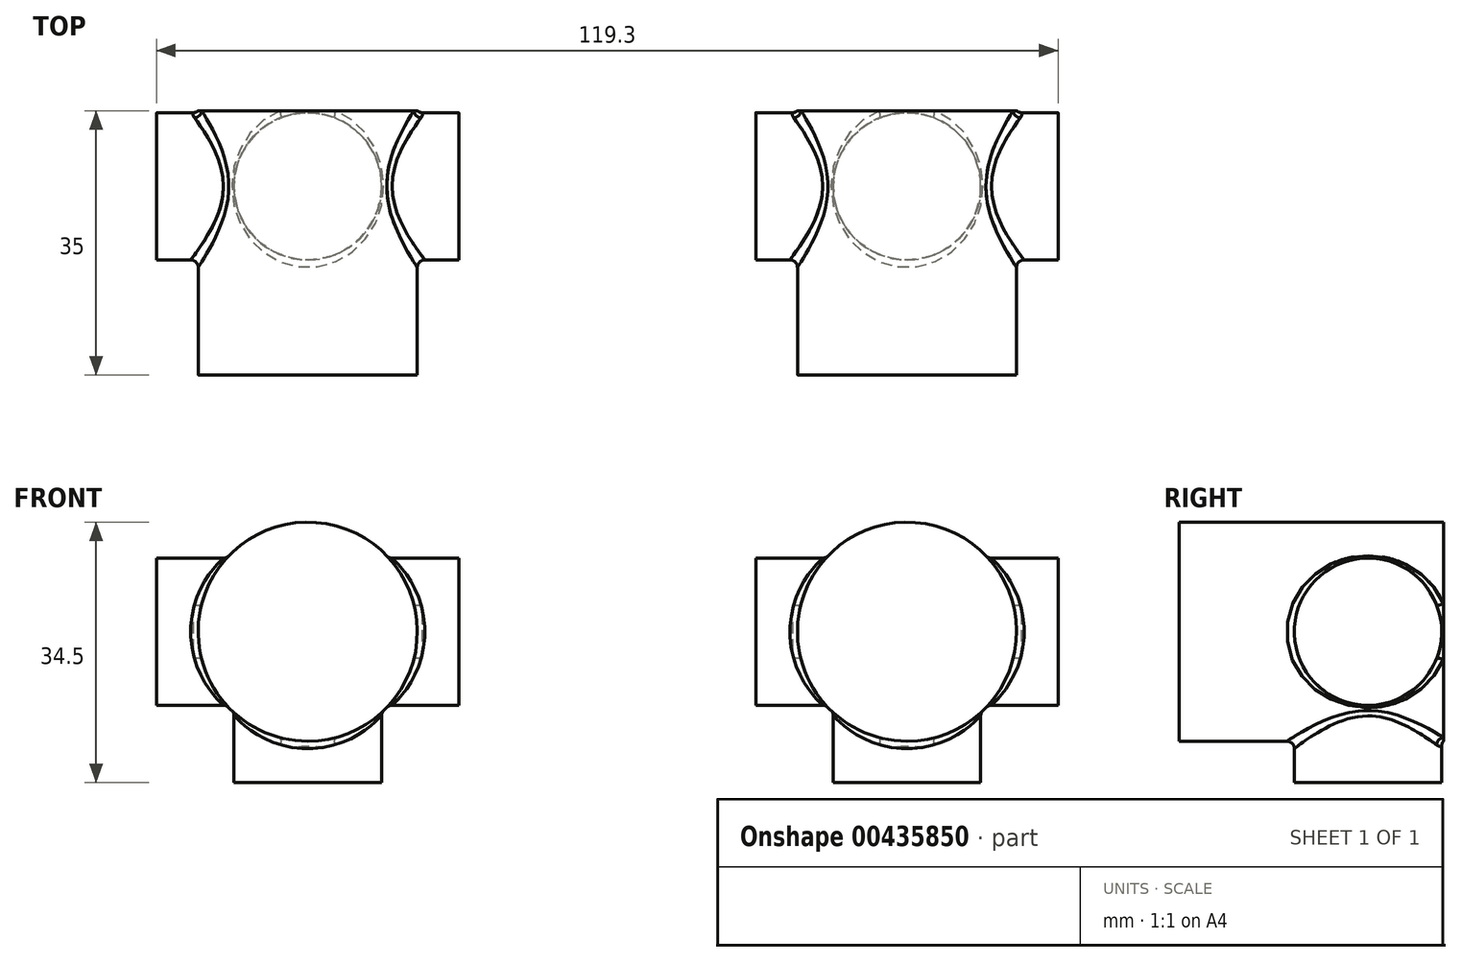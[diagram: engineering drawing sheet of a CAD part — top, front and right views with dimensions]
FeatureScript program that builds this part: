
annotation { "Feature Type Name" : "Feature", "Feature Type Description" : "" }
export const myFeature = defineFeature(function(context is Context, id is Id, definition is map)
    precondition{}
    {
        {
            var Q0;
            Q0=qCreatedBy(makeId("Front.planeOp"),FACE);
            var sketch = newSketch(context, id + "F0", { "sketchPlane" : qUnion([Q0])});
            skCircle(sketch, "E0", {"center": v(0, 0) * mm, "radius": 14.5 * mm});
            skSolve(sketch);
        }
        {
            var Q0;
            Q0 = qSketchRegion(id + "F0", true);
            extrude(context, id + "F1", {"entities" : qUnion([Q0]), "depth" : 25 * mm, "hasSecondDirection" : true, "secondDirectionOppositeDirection" : true, "secondDirectionDepth" : 10 * mm});
        }
        {
            var Q0;
            Q0=qCreatedBy(makeId("Right.planeOp"),FACE);
            var sketch = newSketch(context, id + "F2", { "sketchPlane" : qUnion([Q0])});
            skCircle(sketch, "E1", {"center": v(0, 0) * mm, "radius": 9.75 * mm});
            skSolve(sketch);
        }
        {
            var Q0;
            Q0 = qSketchRegion(id + "F2", true);
            extrude(context, id + "F3", {"entities" : qUnion([Q0]), "operationType" : NewBodyOperationType.ADD, "depth" : 20 * mm, "hasSecondDirection" : true, "secondDirectionOppositeDirection" : true, "secondDirectionDepth" : 20 * mm});
        }
        {
            var Q0;
            Q0=qCreatedBy(makeId("Top.planeOp"),FACE);
            var sketch = newSketch(context, id + "F4", { "sketchPlane" : qUnion([Q0])});
            skCircle(sketch, "E2", {"center": v(0, 0) * mm, "radius": 9.75 * mm});
            skSolve(sketch);
        }
        {
            var Q0;
            Q0 = qSketchRegion(id + "F4", true);
            extrude(context, id + "F5", {"entities" : qUnion([Q0]), "operationType" : NewBodyOperationType.ADD, "oppositeDirection" : true, "depth" : 20 * mm});
        }
        {
            var Q0;
            Q0=makeQuery(id+"F5.boolean.opBoolean","INTERSECT",EDGE,{"disambiguationData":[OD(2.0)],"derivedFrom":[makeQuery(id+"F1.opExtrude","SWEPT_FACE",FACE,{"disambiguationData":[OSD([sQuery(id+"F0.wireOp",EDGE,"E0")])]}),makeQuery(id+"F5.opExtrude","SWEPT_FACE",FACE,{"disambiguationData":[OSD([sQuery(id+"F4.wireOp",EDGE,"E2")])]})]});
            var Q1;
            Q1=makeQuery(id+"F5.boolean.opBoolean","SPLIT",EDGE,{"disambiguationData":[OD(1.0)],"derivedFrom":makeQuery(id+"F3.boolean.opBoolean","INTERSECT",EDGE,{"disambiguationData":[OD(0.0)],"derivedFrom":[makeQuery(id+"F1.opExtrude","SWEPT_FACE",FACE,{"disambiguationData":[OSD([sQuery(id+"F0.wireOp",EDGE,"E0")])]}),makeQuery(id+"F3.opExtrude","SWEPT_FACE",FACE,{"disambiguationData":[OSD([sQuery(id+"F2.wireOp",EDGE,"E1")])]})]})});
            var Q2;
            {var subQ1=sQuery(id+"F2.wireOp",EDGE,"E1");Q2=makeQuery(id+"F5.boolean.opBoolean","INTERSECT",EDGE,{"derivedFrom":[makeQuery(id+"F3.boolean.opBoolean","SPLIT",FACE,{"disambiguationData":[TD([makeQuery(id+"F3.opExtrude","CAP_FACE",FACE,{"disambiguationData":[OSD([subQ1])],"isStart":true})])],"derivedFrom":makeQuery(id+"F3.opExtrude","SWEPT_FACE",FACE,{"disambiguationData":[OSD([subQ1])]})}),makeQuery(id+"F5.opExtrude","SWEPT_FACE",FACE,{"disambiguationData":[OSD([sQuery(id+"F4.wireOp",EDGE,"E2")])]})]});}
            var Q3;
            Q3=makeQuery(id+"F5.boolean.opBoolean","SPLIT",EDGE,{"disambiguationData":[OD(1.0)],"derivedFrom":makeQuery(id+"F3.boolean.opBoolean","INTERSECT",EDGE,{"disambiguationData":[OD(1.0)],"derivedFrom":[makeQuery(id+"F1.opExtrude","SWEPT_FACE",FACE,{"disambiguationData":[OSD([sQuery(id+"F0.wireOp",EDGE,"E0")])]}),makeQuery(id+"F3.opExtrude","SWEPT_FACE",FACE,{"disambiguationData":[OSD([sQuery(id+"F2.wireOp",EDGE,"E1")])]})]})});
            var Q4;
            {var subQ1=sQuery(id+"F2.wireOp",EDGE,"E1");Q4=makeQuery(id+"F5.boolean.opBoolean","INTERSECT",EDGE,{"derivedFrom":[makeQuery(id+"F3.boolean.opBoolean","SPLIT",FACE,{"disambiguationData":[TD([makeQuery(id+"F3.opExtrude","CAP_FACE",FACE,{"disambiguationData":[OSD([subQ1])],"isStart":false})])],"derivedFrom":makeQuery(id+"F3.opExtrude","SWEPT_FACE",FACE,{"disambiguationData":[OSD([subQ1])]})}),makeQuery(id+"F5.opExtrude","SWEPT_FACE",FACE,{"disambiguationData":[OSD([sQuery(id+"F4.wireOp",EDGE,"E2")])]})]});}
            var Q5;
            Q5=makeQuery(id+"F5.boolean.opBoolean","INTERSECT",EDGE,{"disambiguationData":[OD(1.0)],"derivedFrom":[makeQuery(id+"F1.opExtrude","SWEPT_FACE",FACE,{"disambiguationData":[OSD([sQuery(id+"F0.wireOp",EDGE,"E0")])]}),makeQuery(id+"F5.opExtrude","SWEPT_FACE",FACE,{"disambiguationData":[OSD([sQuery(id+"F4.wireOp",EDGE,"E2")])]})]});
            fillet(context, id + "F6", {"entities" : qUnion([Q0, Q1, Q2, Q3, Q4, Q5]), "radius" : 1 * mm, "tangentPropagation" : true, "allowEdgeOverflow" : false});
        }
        {
            var Q0;
            Q0=makeQuery(id+"F1.opExtrude","SWEPT_BODY",BODY,{"disambiguationData":[OSD([sQuery(id+"F0.wireOp",EDGE,"E0")])]});
            transform(context, id + "F7", {"entities" : qUnion([Q0]), "transformType" : TransformType.TRANSLATION_3D, "dx" : 79.3 * mm, "dy" : 0 * mm, "dz" : 0 * mm, "makeCopy" : true});
        }
    });
